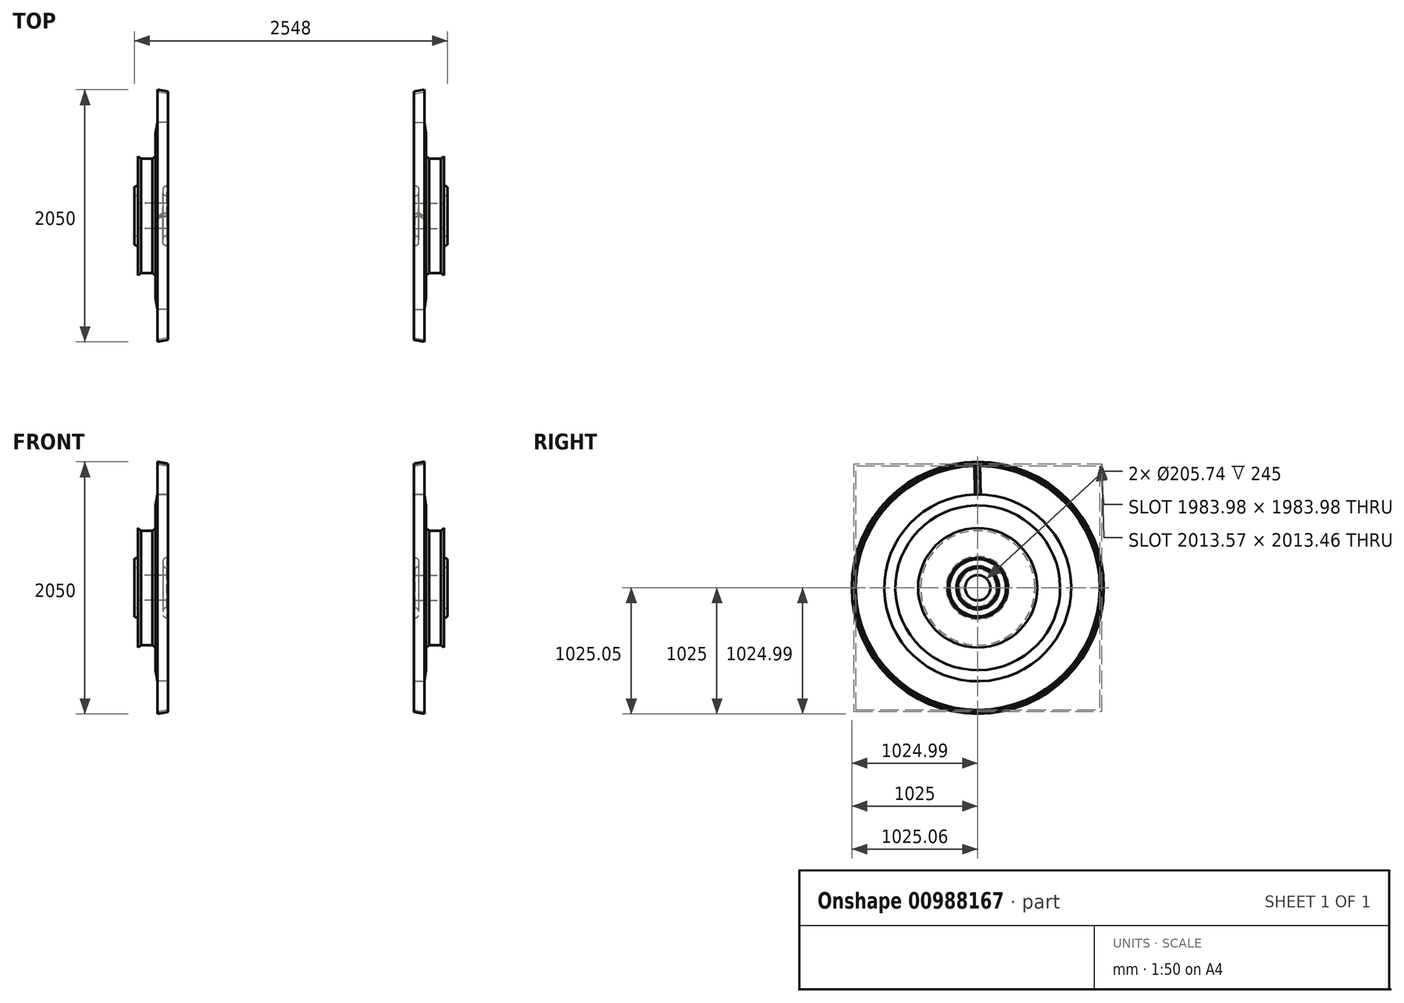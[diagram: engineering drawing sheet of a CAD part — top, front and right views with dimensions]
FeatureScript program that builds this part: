
annotation { "Feature Type Name" : "Feature", "Feature Type Description" : "" }
export const myFeature = defineFeature(function(context is Context, id is Id, definition is map)
    precondition{}
    {
        {
            var Q0;
            Q0=qCreatedBy(makeId("Top.planeOp"),FACE);
            var sketch = newSketch(context, id + "F0", { "sketchPlane" : qUnion([Q0])});
            skLineSegment(sketch, "E0", {"start": v(-458.73, 0) * mm, "end": v(0, 0) * mm, "construction": true});
            skLineSegment(sketch, "E1", {"start": v(0, 760) * mm, "end": v(-85, 760) * mm});
            skLineSegment(sketch, "E2", {"start": v(-125, 465) * mm, "end": v(-220, 465) * mm});
            skLineSegment(sketch, "E3", {"start": v(-220, 465) * mm, "end": v(-245, 485) * mm});
            skLineSegment(sketch, "E4", {"start": v(-245, 485) * mm, "end": v(-245, 243.87) * mm});
            skLineSegment(sketch, "E5", {"start": v(-245, 102.87) * mm, "end": v(0, 102.87) * mm});
            skLineSegment(sketch, "E6", {"start": v(0, 102.87) * mm, "end": v(0, 157.87) * mm});
            skLineSegment(sketch, "E7", {"start": v(-85, 1025) * mm, "end": v(-85, 1007) * mm});
            skLineSegment(sketch, "E8", {"start": v(-85, 1007) * mm, "end": v(0, 992) * mm});
            skLineSegment(sketch, "E9", {"start": v(0, 992) * mm, "end": v(0, 1010) * mm});
            skLineSegment(sketch, "E10", {"start": v(0, 1010) * mm, "end": v(-85, 1025) * mm});
            skLineSegment(sketch, "E11", {"start": v(-85, 760) * mm, "end": v(-85, 1007) * mm, "construction": true});
            skLineSegment(sketch, "E12", {"start": v(-100, 485) * mm, "end": v(-100, 670) * mm});
            skLineSegment(sketch, "E13", {"start": v(-100, 670) * mm, "end": v(-85, 760) * mm});
            skLineSegment(sketch, "E14", {"start": v(-100, 485) * mm, "end": v(-125, 465) * mm});
            skLineSegment(sketch, "E15", {"start": v(-100, 485) * mm, "end": v(-245, 485) * mm, "construction": true});
            skArc(sketch, "E16", {"start": v(-245, 161.87) * mm, "mid": v(-260.7, 165) * mm, "end": v(-274, 173.89) * mm});
            skLineSegment(sketch, "E17", {"start": v(-274, 231.85) * mm, "end": v(-274, 173.89) * mm});
            skArc(sketch, "E18.trimOffspring", {"start": v(-274, 231.85) * mm, "mid": v(-260.7, 240.75) * mm, "end": v(-245, 243.87) * mm});
            skLineSegment(sketch, "E19.trimOffspring", {"start": v(-245, 161.87) * mm, "end": v(-245, 102.87) * mm});
            skArc(sketch, "E20", {"start": v(-245, 161.87) * mm, "mid": v(-286, 202.87) * mm, "end": v(-245, 243.87) * mm, "construction": true});
            skLineSegment(sketch, "E21", {"start": v(-245, 202.87) * mm, "end": v(0, 202.87) * mm, "construction": true});
            skArc(sketch, "E22", {"start": v(0, 157.87) * mm, "mid": v(-22.53, 163.91) * mm, "end": v(-39, 180.42) * mm});
            skLineSegment(sketch, "E23", {"start": v(-39, 225.32) * mm, "end": v(-39, 180.42) * mm});
            skArc(sketch, "E24.trimOffspring", {"start": v(-39, 225.32) * mm, "mid": v(-22.53, 241.83) * mm, "end": v(0, 247.87) * mm});
            skLineSegment(sketch, "E25.trimOffspring", {"start": v(0, 247.87) * mm, "end": v(0, 760) * mm});
            skArc(sketch, "E26", {"start": v(0, 157.87) * mm, "mid": v(-45, 202.87) * mm, "end": v(0, 247.87) * mm, "construction": true});
            skSolve(sketch);
        }
        {
            var Q0;
            Q0=makeQuery(id+"F0.imprint","IMPRINT",FACE,{"disambiguationData":[TD([[makeQuery(id+"F0.imprint","IMPRINT",EDGE,{"derivedFrom":sQuery(id+"F0.wireOp",EDGE,"E7")}),1.0]])]});
            var Q1;
            Q1=makeQuery(id+"F0.imprint","IMPRINT",FACE,{"disambiguationData":[TD([[makeQuery(id+"F0.imprint","IMPRINT",EDGE,{"derivedFrom":sQuery(id+"F0.wireOp",EDGE,"E1")}),1.0]])]});
            var Q2;
            Q2=sQuery(id+"F0.wireOp",EDGE,"E0");
            revolve(context, id + "F1", {"surfaceOperationType" : NewSurfaceOperationType.NEW, "entities" : qUnion([Q0, Q1]), "axis" : qUnion([Q2]), "revolveType" : RevolveType.FULL});
        }
        {
            var Q0;
            Q0=makeQuery(id+"F1.opRevolve","SWEPT_EDGE",EDGE,{"disambiguationData":[OSD([sQuery(id+"F0.wireOp",EDGE,"E24.trimOffspring"),sQuery(id+"F0.wireOp",EDGE,"E25.trimOffspring")])]});
            var Q1;
            Q1=makeQuery(id+"F1.opRevolve","SWEPT_EDGE",EDGE,{"disambiguationData":[OSD([sQuery(id+"F0.wireOp",EDGE,"E6"),sQuery(id+"F0.wireOp",EDGE,"E22")])]});
            chamfer(context, id + "F2", {"entities" : qUnion([Q0, Q1]), "width" : 9 * mm, "tangentPropagation" : true});
        }
        {
            var Q0;
            Q0=qCreatedBy(makeId("Right.planeOp"),FACE);
            var sketch = newSketch(context, id + "F3", { "sketchPlane" : qUnion([Q0])});
            skLineSegment(sketch, "E27", {"start": v(0, 0) * mm, "end": v(0, 760) * mm, "construction": true});
            skLineSegment(sketch, "E28", {"start": v(0, 0) * mm, "end": v(0, 1010) * mm, "construction": true});
            skCircle(sketch, "E29.0", {"center": v(0, 0) * mm, "radius": 1010 * mm, "construction": true});
            skCircle(sketch, "E30.0", {"center": v(0, 0) * mm, "radius": 760 * mm, "construction": true});
            skSolve(sketch);
        }
        {
            var Q0;
            Q0=qCreatedBy(makeId("Front.planeOp"),FACE);
            var sketch = newSketch(context, id + "F4", { "sketchPlane" : qUnion([Q0])});
            skLineSegment(sketch, "E31", {"start": v(-85, 1025) * mm, "end": v(0, 1010) * mm, "construction": true});
            skLineSegment(sketch, "E32", {"start": v(-42.5, 1017.5) * mm, "end": v(-56.24, 939.67) * mm, "construction": true});
            skSolve(sketch);
        }
        {
            var Q0;
            Q0=sQuery(id+"F4.wireOp",EDGE,"E31");
            cPoint(context, id + "F5", {"entities" : qUnion([Q0]), "parameter" : 0.5});
        }
        {
            var Q0;
            Q0 = qCreatedBy(id + "F5" ,VERTEX);
            var Q1;
            Q1=sQuery(id+"F4.wireOp",EDGE,"E32");
            cPlane(context, id + "F6", {"entities" : qUnion([Q0, Q1]), "cplaneType" : CPlaneType.LINE_POINT, "offset" : 25 * mm, "width" : 150 * mm, "height" : 150 * mm});
        }
        {
            var Q0;
            Q0=sQuery(id+"F3.wireOp",VERTEX,"E27.end");
            var Q1;
            Q1=sQuery(id+"F3.wireOp",EDGE,"E28");
            cPlane(context, id + "F7", {"entities" : qUnion([Q0, Q1]), "cplaneType" : CPlaneType.LINE_POINT, "offset" : 25 * mm, "width" : 150 * mm, "height" : 150 * mm});
        }
        {
            var Q0;
            Q0=qCreatedBy(id+"F7.planeOp",FACE);
            cPlane(context, id + "F8", {"entities" : qUnion([Q0]), "cplaneType" : CPlaneType.OFFSET, "offset" : 1 * mm, "oppositeDirection" : true, "width" : 150 * mm, "height" : 150 * mm});
        }
        {
            var Q0;
            Q0=qCreatedBy(id+"F6.planeOp",FACE);
            cPlane(context, id + "F9", {"entities" : qUnion([Q0]), "cplaneType" : CPlaneType.OFFSET, "offset" : 5 * mm, "width" : 150 * mm, "height" : 150 * mm});
        }
        {
            var Q0;
            Q0=qCreatedBy(id+"F8.planeOp",FACE);
            var sketch = newSketch(context, id + "F10", { "sketchPlane" : qUnion([Q0])});
            skLineSegment(sketch, "E33.0", {"start": v(-85, -760) * mm, "end": v(-85, 760) * mm, "construction": true});
            skLineSegment(sketch, "E34.0", {"start": v(0, 760) * mm, "end": v(0, -760) * mm, "construction": true});
            skLineSegment(sketch, "E35", {"start": v(0, 0) * mm, "end": v(0, 15) * mm});
            skLineSegment(sketch, "E36", {"start": v(-85, -11.9) * mm, "end": v(-85, -21.9) * mm});
            skFitSpline(sketch, "E37", {"points": [v(0, 15) * mm, v(-30.5, 23.18) * mm, v(-56.1, 15) * mm, v(-85, -11.9) * mm], "startDerivative": vector(-98.33, 77.82) * mm, "endDerivative": vector(-58.12, -78.29) * mm});
            skFitSpline(sketch, "E38", {"points": [v(0, 0) * mm, v(-15.4, -5.27) * mm, v(-34.8, 2.04) * mm, v(-85, -21.9) * mm], "startDerivative": vector(-36.35, -51.97) * mm, "endDerivative": vector(-105.16, -83.49) * mm});
            skSolve(sketch);
        }
        {
            var Q0;
            Q0=qCreatedBy(id+"F9.planeOp",FACE);
            var sketch = newSketch(context, id + "F11", { "sketchPlane" : qUnion([Q0])});
            skLineSegment(sketch, "E39", {"start": v(-260.95, 28.43) * mm, "end": v(-260.95, 18.43) * mm});
            skLineSegment(sketch, "E40", {"start": v(-174.64, 6.55) * mm, "end": v(-174.64, -8.45) * mm});
            skFitSpline(sketch, "E41", {"points": [v(-174.64, 6.55) * mm, v(-191.16, 11.32) * mm, v(-211.6, 4.64) * mm, v(-260.95, 28.43) * mm], "startDerivative": vector(-65.47, 68.6) * mm, "endDerivative": vector(-133.62, 88.3) * mm});
            skFitSpline(sketch, "E42", {"points": [v(-174.64, -8.45) * mm, v(-206.37, -17.35) * mm, v(-231.59, -8.73) * mm, v(-260.95, 18.43) * mm], "startDerivative": vector(-80.99, -68.84) * mm, "endDerivative": vector(-73.9, 76.03) * mm});
            skLineSegment(sketch, "E43", {"start": v(-260.95, -101.9) * mm, "end": v(-260.95, 101.9) * mm, "construction": true});
            skLineSegment(sketch, "E44", {"start": v(-174.64, 101.14) * mm, "end": v(-174.64, -101.14) * mm, "construction": true});
            skPoint(sketch, "E45", {"position": v(-260.95, 0) * mm});
            skSolve(sketch);
        }
        {
            var Q2;
            Q2=qSketchRegion(id+"F10",true);
            var Q3;
            Q3=qSketchRegion(id+"F11",true);
            loft(context, id + "F12", {"operationType" : NewBodyOperationType.ADD, "sheetProfilesArray" : [{ "sheetProfileEntities" : qUnion([Q2]) }, { "sheetProfileEntities" : qUnion([Q3]) }]});
        }
        {
            var Q0;
            Q0=qCreatedBy(makeId("Right.planeOp"),FACE);
            cPlane(context, id + "F13", {"entities" : qUnion([Q0]), "cplaneType" : CPlaneType.OFFSET, "offset" : 1000 * mm, "width" : 150 * mm, "height" : 150 * mm});
        }
        {
            var Q0;
            Q0=makeQuery(id+"F1.opRevolve","SWEPT_BODY",BODY,{"disambiguationData":[OSD([sQuery(id+"F0.wireOp",EDGE,"E1"),sQuery(id+"F0.wireOp",EDGE,"E2"),sQuery(id+"F0.wireOp",EDGE,"E3"),sQuery(id+"F0.wireOp",EDGE,"E4"),sQuery(id+"F0.wireOp",EDGE,"E5"),sQuery(id+"F0.wireOp",EDGE,"E6"),sQuery(id+"F0.wireOp",EDGE,"E12"),sQuery(id+"F0.wireOp",EDGE,"E13"),sQuery(id+"F0.wireOp",EDGE,"E14"),sQuery(id+"F0.wireOp",EDGE,"E16"),sQuery(id+"F0.wireOp",EDGE,"E17"),sQuery(id+"F0.wireOp",EDGE,"E18.trimOffspring"),sQuery(id+"F0.wireOp",EDGE,"E19.trimOffspring"),sQuery(id+"F0.wireOp",EDGE,"E22"),sQuery(id+"F0.wireOp",EDGE,"E23"),sQuery(id+"F0.wireOp",EDGE,"E24.trimOffspring"),sQuery(id+"F0.wireOp",EDGE,"E25.trimOffspring")])]});
            var Q1;
            Q1=qCreatedBy(id+"F13.planeOp",FACE);
            mirror(context, id + "F14", {"entities" : qUnion([Q0]), "mirrorPlane" : qUnion([Q1])});
        }
    });
